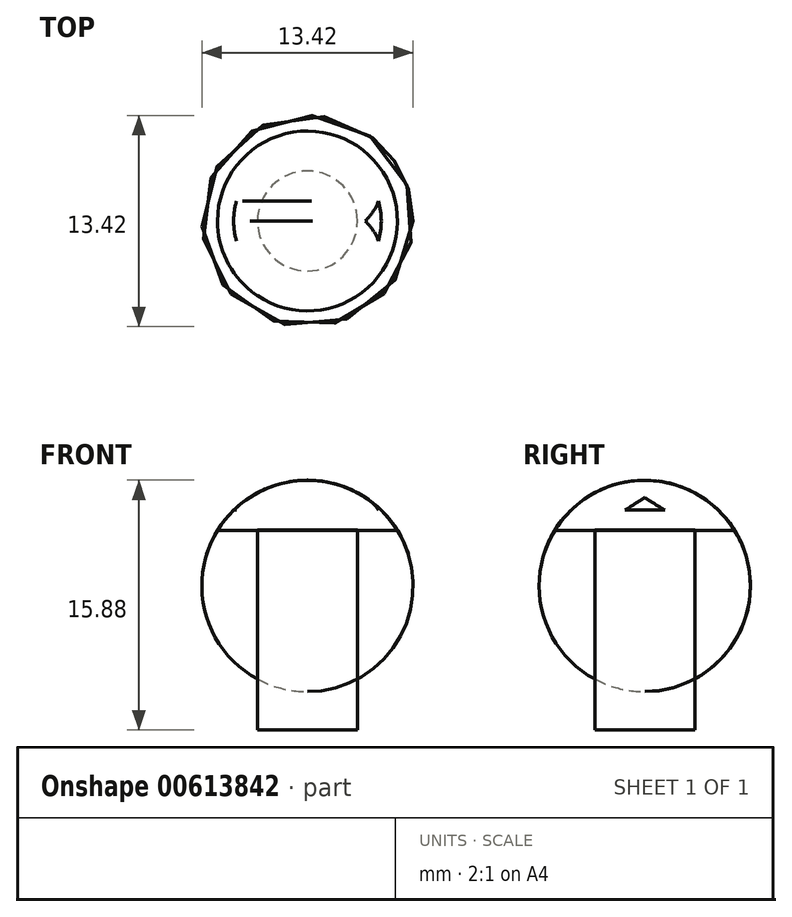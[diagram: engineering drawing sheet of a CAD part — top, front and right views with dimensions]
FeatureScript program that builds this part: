
annotation { "Feature Type Name" : "Feature", "Feature Type Description" : "" }
export const myFeature = defineFeature(function(context is Context, id is Id, definition is map)
    precondition{}
    {
        {
            var Q0;
            Q0=qCreatedBy(makeId("Front.planeOp"),FACE);
            var sketch = newSketch(context, id + "F0", { "sketchPlane" : qUnion([Q0])});
            skLineSegment(sketch, "E0", {"start": v(0, 0) * mm, "end": v(0, 15.88) * mm});
            skLineSegment(sketch, "E1", {"start": v(3.18, 0) * mm, "end": v(3.18, 12.7) * mm});
            skPoint(sketch, "E2", {"position": v(5.72, 12.69) * mm});
            skLineSegment(sketch, "E3", {"start": v(3.18, 12.7) * mm, "end": v(5.72, 12.69) * mm});
            skArc(sketch, "E4.trimOffspring", {"start": v(5.72, 12.69) * mm, "mid": v(3.27, 15.02) * mm, "end": v(0, 15.88) * mm});
            skLineSegment(sketch, "E5", {"start": v(0, 0) * mm, "end": v(3.18, 0) * mm});
            skSolve(sketch);
        }
        {
            var Q0;
            Q0=makeQuery(id+"F0.imprint","IMPRINT",FACE,{"disambiguationData":[TD([[makeQuery(id+"F0.imprint","IMPRINT",EDGE,{"derivedFrom":sQuery(id+"F0.wireOp",EDGE,"E0")}),-1.0]])]});
            var Q1;
            Q1=sQuery(id+"F0.wireOp",EDGE,"E0");
            revolve(context, id + "F1", {"entities" : qUnion([Q0]), "axis" : qUnion([Q1]), "revolveType" : RevolveType.FULL});
        }
        {
            var Q0;
            Q0=qCreatedBy(makeId("Top.planeOp"),FACE);
            cPlane(context, id + "F2", {"entities" : qUnion([Q0]), "cplaneType" : CPlaneType.OFFSET, "offset" : 13.97 * mm, "width" : 152.4 * mm, "height" : 152.4 * mm});
        }
        {
            var Q0;
            Q0=qCreatedBy(id+"F2.planeOp",FACE);
            var sketch = newSketch(context, id + "F3", { "sketchPlane" : qUnion([Q0])});
            skLineSegment(sketch, "E6.bottom", {"start": v(-5.08, 1.27) * mm, "end": v(5.08, 1.27) * mm});
            skLineSegment(sketch, "E6.top", {"start": v(-5.08, -1.27) * mm, "end": v(5.08, -1.27) * mm});
            skLineSegment(sketch, "E6.left", {"start": v(-5.08, 1.27) * mm, "end": v(-5.08, -1.27) * mm});
            skLineSegment(sketch, "E6.right", {"start": v(5.08, 1.27) * mm, "end": v(5.08, -1.27) * mm});
            skPoint(sketch, "E6.middle", {"position": v(0, 0) * mm});
            skSolve(sketch);
        }
        {
            var Q0;
            Q0 = qSketchRegion(id + "F3", true);
            extrude(context, id + "F4", {"entities" : qUnion([Q0]), "operationType" : NewBodyOperationType.REMOVE, "depth" : 6.48 * mm, "offsetDistance" : 25.4 * mm});
        }
    });
